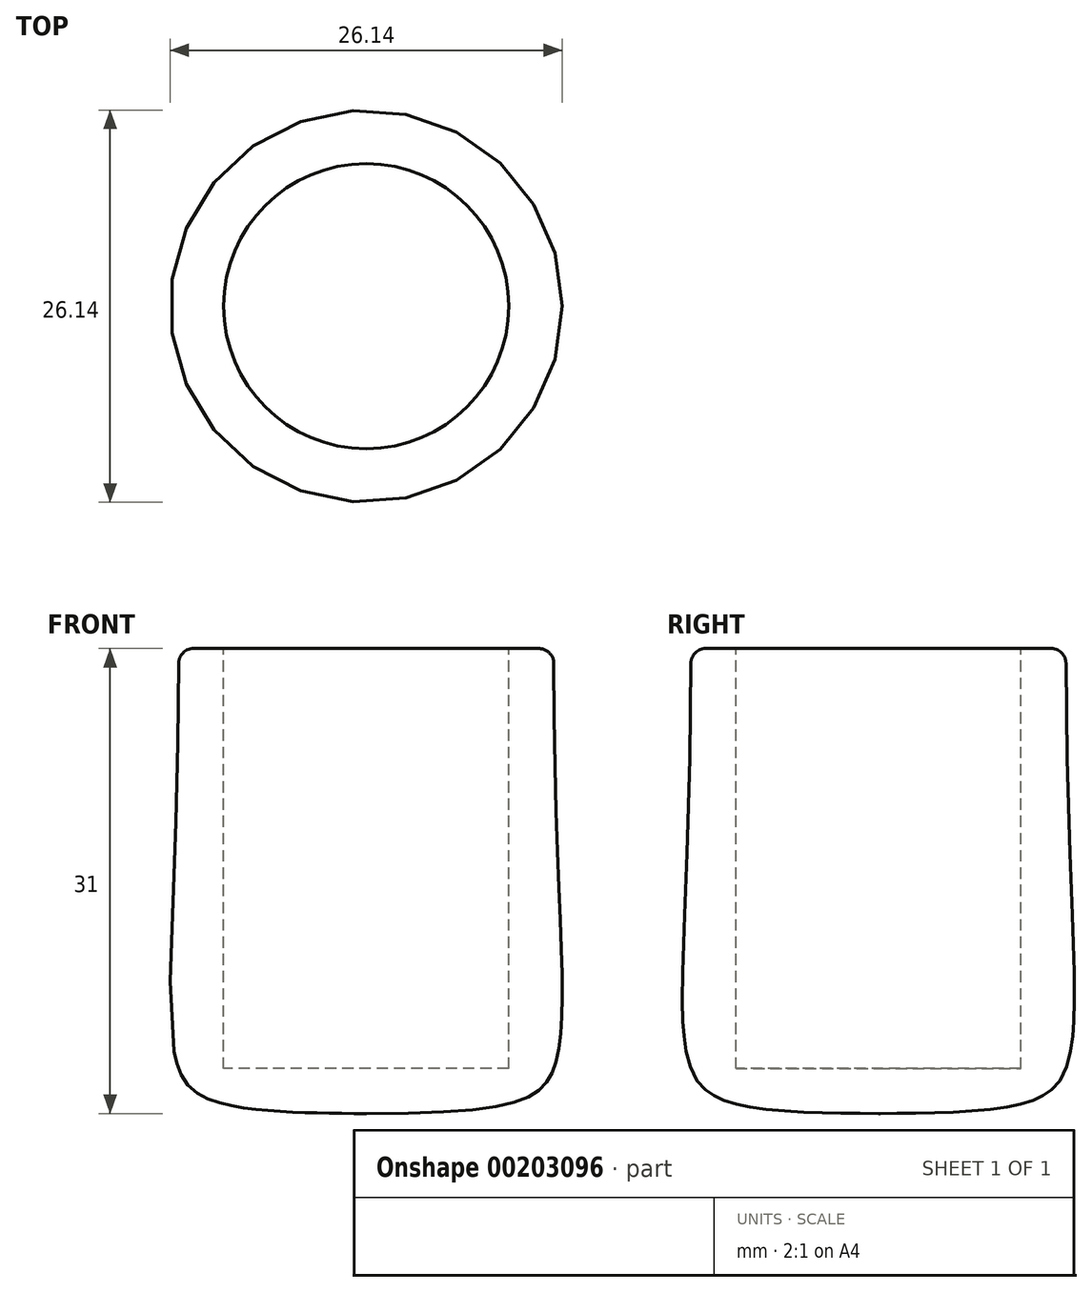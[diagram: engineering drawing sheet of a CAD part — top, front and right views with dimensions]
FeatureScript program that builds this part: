
annotation { "Feature Type Name" : "Feature", "Feature Type Description" : "" }
export const myFeature = defineFeature(function(context is Context, id is Id, definition is map)
    precondition{}
    {
        {
            var Q0;
            Q0=qCreatedBy(makeId("Front.planeOp"),FACE);
            var sketch = newSketch(context, id + "F0", { "sketchPlane" : qUnion([Q0])});
            skLineSegment(sketch, "E0", {"start": v(0, 0) * mm, "end": v(9.5, 0) * mm});
            skLineSegment(sketch, "E1", {"start": v(9.5, 0) * mm, "end": v(9.5, 28) * mm});
            skLineSegment(sketch, "E2", {"start": v(0, 0) * mm, "end": v(0, -3) * mm});
            skLineSegment(sketch, "E3", {"start": v(9.5, 28) * mm, "end": v(12.5, 28) * mm});
            skFitSpline(sketch, "E4", {"points": [v(0, -3) * mm, v(12.5, 0) * mm, v(12.5, 28) * mm], "startDerivative": vector(71.3, 0) * mm, "endDerivative": vector(0, 89.6) * mm});
            skSolve(sketch);
        }
        {
            var Q0;
            Q0 = qSketchRegion(id + "F0", true);
            var Q1;
            Q1=sQuery(id+"F0.wireOp",EDGE,"E2");
            revolve(context, id + "F1", {"surfaceOperationType" : NewSurfaceOperationType.NEW, "entities" : qUnion([Q0]), "axis" : qUnion([Q1]), "revolveType" : RevolveType.FULL});
        }
        {
            var Q0;
            Q0=makeQuery(id+"F1.opRevolve","SWEPT_EDGE",EDGE,{"disambiguationData":[OSD([sQuery(id+"F0.wireOp",EDGE,"E3"),sQuery(id+"F0.wireOp",EDGE,"E4")])]});
            fillet(context, id + "F2", {"entities" : qUnion([Q0]), "tangentPropagation" : true, "radius" : 1 * mm, "defaultsChanged" : false, "vertexSettings" : [], "allowEdgeOverflow" : false});
        }
    });
